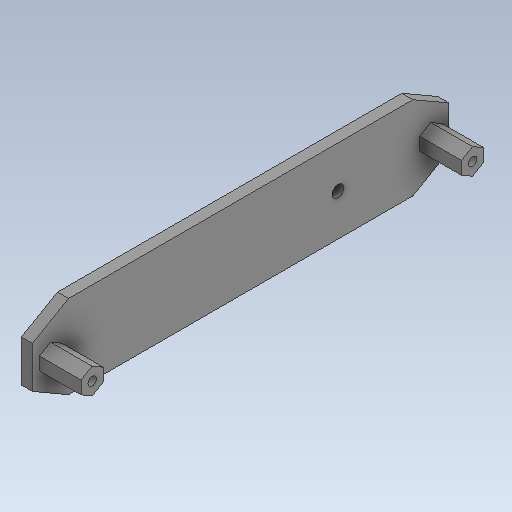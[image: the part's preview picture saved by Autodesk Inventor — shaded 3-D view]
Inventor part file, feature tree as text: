
AUTODESK INVENTOR PART (.ipt)
format: ipt  version: 2020 (Build 240168000, 168)  size: 256,000 bytes
history: native  units: in
note: dims shown in document units (in); Inventor stores cm internally (conversion verified against a paired STEP export)
features: extrude x6, sketch x6, plane x1
ambient origin geometry x8: Origin, YZ Plane, XZ Plane, XY Plane, X Axis, Y Axis, Z Axis, Center Point
bodies: Solid1 (feature_tree)
feature tree (13):
  extrude  "Extrusion1"  Depth=5.9055in
  extrude  "Extrusion3"  TaperAngle=0.0deg  [1 undecoded]
  extrude  "Extrusion4"  Depth=0.5906in
  plane  "Work Plane1"
  extrude  "Extrusion5"  Depth=0.122in
  extrude  "Extrusion6"  Depth=0.2402in
  extrude  "Extrusion7"  [1 undecoded]
  sketch  "Sketch1"  dims[d0=1.1811in d1=5.9055in]
  sketch  "Sketch2"  dims[d2=0.1575in d3=0.0in]
  sketch  "Sketch3"  dims[d8=0.315in d9=0.5906in]
  sketch  "Sketch4"  dims[d10=0.0in d12=0.122in]
  sketch  "Sketch5"  dims[d13=0.0in d14=0.0in d15=0.2402in]
  sketch  "Sketch8"  dims[d16=0.0866in d17=-0.2233in d18=-0.3937in d19=0.0866in d20=0.0in d26=1.5748in d27=0.1654in d30=0.0in d31=0.0in]
note: 2 required parameter values undecoded (feature->parameter linkage not recoverable at this tier; creation-order binding heuristic only, values carry confidence <= 0.55)
